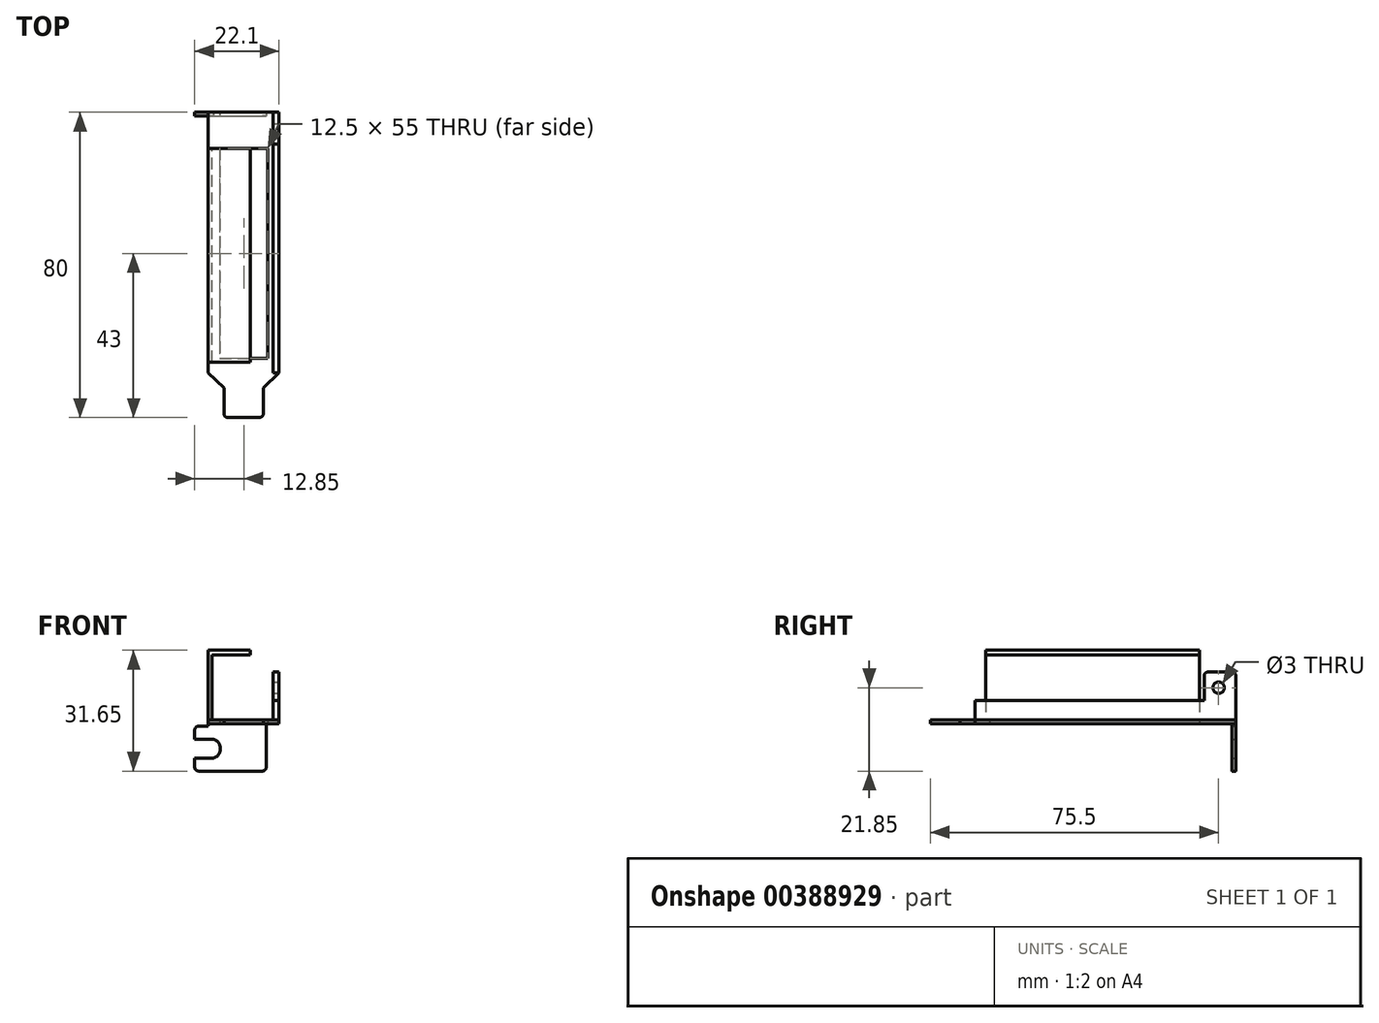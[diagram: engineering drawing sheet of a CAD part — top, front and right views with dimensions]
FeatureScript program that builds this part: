
annotation { "Feature Type Name" : "Feature", "Feature Type Description" : "" }
export const myFeature = defineFeature(function(context is Context, id is Id, definition is map)
    precondition{}
    {
        {
            var Q0;
            Q0=qCreatedBy(makeId("Top.planeOp"),FACE);
            var sketch = newSketch(context, id + "F0", { "sketchPlane" : qUnion([Q0])});
            skLineSegment(sketch, "E0", {"start": v(-1, 0) * mm, "end": v(-9.3, 0) * mm});
            skLineSegment(sketch, "E1", {"start": v(-10.3, 1) * mm, "end": v(-10.3, 7.8) * mm});
            skLineSegment(sketch, "E2", {"start": v(-10.3, 7.8) * mm, "end": v(-14.45, 11.7) * mm});
            skLineSegment(sketch, "E3", {"start": v(-14.45, 11.7) * mm, "end": v(-14.45, 73.4) * mm});
            skLineSegment(sketch, "E4", {"start": v(0, 1) * mm, "end": v(0, 7.8) * mm});
            skLineSegment(sketch, "E5", {"start": v(0, 7.8) * mm, "end": v(4.15, 11.7) * mm});
            skLineSegment(sketch, "E6", {"start": v(4.15, 11.7) * mm, "end": v(4.15, 73.4) * mm});
            skLineSegment(sketch, "E7", {"start": v(-14.45, 11.7) * mm, "end": v(4.15, 11.7) * mm, "construction": true});
            skLineSegment(sketch, "E8", {"start": v(-14.45, 73.4) * mm, "end": v(-14.45, 80) * mm});
            skLineSegment(sketch, "E9", {"start": v(-14.45, 80) * mm, "end": v(0.75, 80) * mm});
            skLineSegment(sketch, "E10", {"start": v(-14.45, 80) * mm, "end": v(-47.1, 80) * mm, "construction": true});
            skLineSegment(sketch, "E11", {"start": v(-47.1, 80) * mm, "end": v(-47.1, 0) * mm, "construction": true});
            skLineSegment(sketch, "E12", {"start": v(-47.1, 0) * mm, "end": v(-10.3, 0) * mm, "construction": true});
            skLineSegment(sketch, "E13", {"start": v(-14.45, 11.7) * mm, "end": v(-37.1, 11.7) * mm, "construction": true});
            skLineSegment(sketch, "E14", {"start": v(-37.1, 11.7) * mm, "end": v(-37.1, 80) * mm, "construction": true});
            skLineSegment(sketch, "E15", {"start": v(0.75, 80) * mm, "end": v(0.75, 76.5) * mm});
            skLineSegment(sketch, "E16", {"start": v(0.75, 76.5) * mm, "end": v(4.15, 73.4) * mm});
            skPoint(sketch, "E17.visualSharp", {"position": v(0, 0) * mm});
            skArc(sketch, "E17.filletArc", {"start": v(-1, 0) * mm, "mid": v(-0.3, 0.3) * mm, "end": v(0, 1) * mm});
            skPoint(sketch, "E18.visualSharp", {"position": v(-10.3, 0) * mm});
            skArc(sketch, "E18.filletArc", {"start": v(-10.3, 1) * mm, "mid": v(-10, 0.3) * mm, "end": v(-9.3, 0) * mm});
            skLineSegment(sketch, "E19", {"start": v(4.15, 73.4) * mm, "end": v(4.15, 80) * mm, "construction": true});
            skLineSegment(sketch, "E20", {"start": v(4.15, 80) * mm, "end": v(0.75, 80) * mm, "construction": true});
            skSolve(sketch);
        }
        {
            var Q0;
            Q0 = qSketchRegion(id + "F0", true);
            extrude(context, id + "F1", {"entities" : qUnion([Q0]), "depth" : 1 * mm});
        }
        {
            var Q0;
            Q0=makeQuery(id+"F1.opExtrude","SWEPT_FACE",FACE,{"disambiguationData":[OSD([sQuery(id+"F0.wireOp",EDGE,"E9")])]});
            var sketch = newSketch(context, id + "F2", { "sketchPlane" : qUnion([Q0])});
            skLineSegment(sketch, "E21", {"start": v(14.45, 1) * mm, "end": v(14.45, -0.7) * mm});
            skLineSegment(sketch, "E22", {"start": v(14.45, -0.7) * mm, "end": v(16.95, -0.7) * mm});
            skLineSegment(sketch, "E23", {"start": v(17.95, -1.7) * mm, "end": v(17.95, -4.1) * mm});
            skLineSegment(sketch, "E24", {"start": v(17.95, -4.1) * mm, "end": v(12.95, -4.1) * mm});
            skLineSegment(sketch, "E25", {"start": v(12.95, -9.05) * mm, "end": v(17.95, -9.05) * mm});
            skLineSegment(sketch, "E26", {"start": v(17.95, -9.05) * mm, "end": v(17.95, -11.45) * mm});
            skPoint(sketch, "E27", {"position": v(-0.75, 0.5) * mm});
            skLineSegment(sketch, "E28", {"start": v(16.95, -12.45) * mm, "end": v(0.25, -12.45) * mm});
            skLineSegment(sketch, "E29", {"start": v(-0.75, -11.45) * mm, "end": v(-0.75, 1) * mm});
            skLineSegment(sketch, "E30", {"start": v(11.25, -6.57) * mm, "end": v(11.25, -2.4) * mm, "construction": true});
            skLineSegment(sketch, "E31", {"start": v(11.25, -2.4) * mm, "end": v(17.95, -2.4) * mm, "construction": true});
            skArc(sketch, "E32", {"start": v(12.95, -4.1) * mm, "mid": v(11.25, -6.58) * mm, "end": v(12.95, -9.05) * mm});
            skPoint(sketch, "E33.visualSharp", {"position": v(17.95, -0.7) * mm});
            skArc(sketch, "E33.filletArc", {"start": v(17.95, -1.7) * mm, "mid": v(17.66, -1) * mm, "end": v(16.95, -0.7) * mm});
            skPoint(sketch, "E34.visualSharp", {"position": v(17.95, -12.45) * mm});
            skArc(sketch, "E34.filletArc", {"start": v(16.95, -12.45) * mm, "mid": v(17.66, -12.16) * mm, "end": v(17.95, -11.45) * mm});
            skPoint(sketch, "E35.visualSharp", {"position": v(-0.75, -12.45) * mm});
            skArc(sketch, "E35.filletArc", {"start": v(-0.75, -11.45) * mm, "mid": v(-0.46, -12.16) * mm, "end": v(0.25, -12.45) * mm});
            skLineSegment(sketch, "E36", {"start": v(-0.75, -9.25) * mm, "end": v(2.45, -9.25) * mm, "construction": true});
            skLineSegment(sketch, "E37", {"start": v(2.45, -9.25) * mm, "end": v(2.45, -12.45) * mm, "construction": true});
            skCircle(sketch, "E38", {"center": v(2.45, -9.25) * mm, "radius": 1.15 * mm});
            skSolve(sketch);
        }
        {
            var Q0;
            Q0 = qSketchRegion(id + "F2", true);
            var Q1;
            {var subQ4=sQuery(id+"F2.wireOp",EDGE,"E22");Q1=makeQuery(id+"F2.imprint","IMPRINT",FACE,{"disambiguationData":[TD([[makeQuery(id+"F2.imprint","IMPRINT",EDGE,{"derivedFrom":subQ4}),-1.0]])]});}
            extrude(context, id + "F3", {"entities" : qUnion([Q0, Q1]), "operationType" : NewBodyOperationType.ADD, "oppositeDirection" : true, "depth" : 1 * mm});
        }
        {
            var Q0;
            Q0=makeQuery(id+"F1.opExtrude","CAP_FACE",FACE,{"disambiguationData":[OSD([sQuery(id+"F0.wireOp",EDGE,"E0"),sQuery(id+"F0.wireOp",EDGE,"E1"),sQuery(id+"F0.wireOp",EDGE,"E2"),sQuery(id+"F0.wireOp",EDGE,"E3"),sQuery(id+"F0.wireOp",EDGE,"E4"),sQuery(id+"F0.wireOp",EDGE,"E5"),sQuery(id+"F0.wireOp",EDGE,"E6"),sQuery(id+"F0.wireOp",EDGE,"E8"),sQuery(id+"F0.wireOp",EDGE,"E9"),sQuery(id+"F0.wireOp",EDGE,"E15"),sQuery(id+"F0.wireOp",EDGE,"E16"),sQuery(id+"F0.wireOp",EDGE,"E17.filletArc"),sQuery(id+"F0.wireOp",EDGE,"E18.filletArc")])],"isStart":true});
            var sketch = newSketch(context, id + "F4", { "sketchPlane" : qUnion([Q0])});
            skLineSegment(sketch, "E39.bottom", {"start": v(-11.35, -70.5) * mm, "end": v(1.15, -70.5) * mm});
            skLineSegment(sketch, "E39.top", {"start": v(-11.35, -15.5) * mm, "end": v(1.15, -15.5) * mm});
            skLineSegment(sketch, "E39.left", {"start": v(-11.35, -70.5) * mm, "end": v(-11.35, -15.5) * mm});
            skLineSegment(sketch, "E39.right", {"start": v(1.15, -70.5) * mm, "end": v(1.15, -15.5) * mm});
            skLineSegment(sketch, "E40", {"start": v(1.15, -28.24) * mm, "end": v(4.15, -28.24) * mm, "construction": true});
            skLineSegment(sketch, "E41", {"start": v(-6.24, 0) * mm, "end": v(-6.24, -15.5) * mm, "construction": true});
            skPoint(sketch, "E41.endSnap0", {"position": v(-5.1, -15.5) * mm});
            skSolve(sketch);
        }
        {
            var Q0;
            Q0=makeQuery(id+"F4.imprint","IMPRINT",FACE,{"disambiguationData":[TD([[makeQuery(id+"F4.imprint","IMPRINT",EDGE,{"derivedFrom":sQuery(id+"F4.wireOp",EDGE,"E39.bottom")}),1.0]])]});
            extrude(context, id + "F5", {"entities" : qUnion([Q0]), "operationType" : NewBodyOperationType.REMOVE, "oppositeDirection" : true, "depth" : 1 * mm});
        }
        {
            var Q0;
            Q0=makeQuery(id+"F1.opExtrude","CAP_FACE",FACE,{"disambiguationData":[OSD([sQuery(id+"F0.wireOp",EDGE,"E0"),sQuery(id+"F0.wireOp",EDGE,"E1"),sQuery(id+"F0.wireOp",EDGE,"E2"),sQuery(id+"F0.wireOp",EDGE,"E3"),sQuery(id+"F0.wireOp",EDGE,"E4"),sQuery(id+"F0.wireOp",EDGE,"E5"),sQuery(id+"F0.wireOp",EDGE,"E6"),sQuery(id+"F0.wireOp",EDGE,"E8"),sQuery(id+"F0.wireOp",EDGE,"E9"),sQuery(id+"F0.wireOp",EDGE,"E15"),sQuery(id+"F0.wireOp",EDGE,"E16"),sQuery(id+"F0.wireOp",EDGE,"E17.filletArc"),sQuery(id+"F0.wireOp",EDGE,"E18.filletArc")])],"isStart":false});
            var sketch = newSketch(context, id + "F6", { "sketchPlane" : qUnion([Q0])});
            skLineSegment(sketch, "E42", {"start": v(4.15, 73.4) * mm, "end": v(4.15, 80) * mm});
            skLineSegment(sketch, "E43", {"start": v(4.15, 80) * mm, "end": v(0.75, 80) * mm});
            skLineSegment(sketch, "E44", {"start": v(0.75, 80) * mm, "end": v(0.75, 76.5) * mm});
            skLineSegment(sketch, "E45", {"start": v(0.75, 76.5) * mm, "end": v(4.15, 73.4) * mm});
            skSolve(sketch);
        }
        {
            var Q0;
            Q0 = qSketchRegion(id + "F6", true);
            extrude(context, id + "F7", {"entities" : qUnion([Q0]), "operationType" : NewBodyOperationType.ADD, "oppositeDirection" : true, "depth" : 1 * mm});
        }
        {
            var Q0;
            Q0=makeQuery(id+"F1.opExtrude","SWEPT_FACE",FACE,{"disambiguationData":[OSD([sQuery(id+"F0.wireOp",EDGE,"E6")])]});
            var sketch = newSketch(context, id + "F8", { "sketchPlane" : qUnion([Q0])});
            skLineSegment(sketch, "E46", {"start": v(80, 1) * mm, "end": v(80, 12.5) * mm});
            skLineSegment(sketch, "E47", {"start": v(79, 13.5) * mm, "end": v(72.7, 13.5) * mm});
            skLineSegment(sketch, "E48", {"start": v(71.7, 12.5) * mm, "end": v(71.7, 6) * mm});
            skLineSegment(sketch, "E49", {"start": v(71.7, 6) * mm, "end": v(11.7, 6) * mm});
            skPoint(sketch, "E50.visualSharp", {"position": v(80, 13.5) * mm});
            skArc(sketch, "E50.filletArc", {"start": v(80, 12.5) * mm, "mid": v(79.7, 13.2) * mm, "end": v(79, 13.5) * mm});
            skPoint(sketch, "E51.visualSharp", {"position": v(71.7, 13.5) * mm});
            skArc(sketch, "E51.filletArc", {"start": v(72.7, 13.5) * mm, "mid": v(72, 13.2) * mm, "end": v(71.7, 12.5) * mm});
            skLineSegment(sketch, "E52", {"start": v(75.5, 13.5) * mm, "end": v(75.5, 9.4) * mm, "construction": true});
            skLineSegment(sketch, "E53", {"start": v(11.7, 6) * mm, "end": v(11.7, 1) * mm});
            skLineSegment(sketch, "E54", {"start": v(75.5, 9.4) * mm, "end": v(80, 9.4) * mm, "construction": true});
            skSolve(sketch);
        }
        {
            var Q0;
            {var subQ1=sQuery(id+"F8.wireOp",EDGE,"E47");Q0=makeQuery(id+"F8.imprint","IMPRINT",FACE,{"disambiguationData":[TD([[makeQuery(id+"F8.imprint","IMPRINT",EDGE,{"derivedFrom":subQ1}),1.0]])]});}
            extrude(context, id + "F9", {"entities" : qUnion([Q0]), "oppositeDirection" : true, "depth" : 1.6 * mm});
        }
        {
            var Q0;
            Q0=makeQuery(id+"F7.boolean.opBoolean","MERGE",FACE,{"derivedFrom":[makeQuery(id+"F1.opExtrude","CAP_FACE",FACE,{"disambiguationData":[OSD([sQuery(id+"F0.wireOp",EDGE,"E0"),sQuery(id+"F0.wireOp",EDGE,"E1"),sQuery(id+"F0.wireOp",EDGE,"E2"),sQuery(id+"F0.wireOp",EDGE,"E3"),sQuery(id+"F0.wireOp",EDGE,"E4"),sQuery(id+"F0.wireOp",EDGE,"E5"),sQuery(id+"F0.wireOp",EDGE,"E6"),sQuery(id+"F0.wireOp",EDGE,"E8"),sQuery(id+"F0.wireOp",EDGE,"E9"),sQuery(id+"F0.wireOp",EDGE,"E15"),sQuery(id+"F0.wireOp",EDGE,"E16"),sQuery(id+"F0.wireOp",EDGE,"E17.filletArc"),sQuery(id+"F0.wireOp",EDGE,"E18.filletArc")])],"isStart":false}),makeQuery(id+"F7.opExtrude","CAP_FACE",FACE,{"disambiguationData":[OSD([sQuery(id+"F6.wireOp",EDGE,"E42"),sQuery(id+"F6.wireOp",EDGE,"E43"),sQuery(id+"F6.wireOp",EDGE,"E44"),sQuery(id+"F6.wireOp",EDGE,"E45")])],"isStart":true})]});
            var sketch = newSketch(context, id + "F10", { "sketchPlane" : qUnion([Q0])});
            skLineSegment(sketch, "E55.bottom", {"start": v(-14.45, 14.5) * mm, "end": v(-13.45, 14.5) * mm});
            skLineSegment(sketch, "E55.top", {"start": v(-14.45, 70.5) * mm, "end": v(-13.45, 70.5) * mm});
            skLineSegment(sketch, "E55.left", {"start": v(-14.45, 14.5) * mm, "end": v(-14.45, 70.5) * mm});
            skLineSegment(sketch, "E55.right", {"start": v(-13.45, 14.5) * mm, "end": v(-13.45, 70.5) * mm});
            skLineSegment(sketch, "E56", {"start": v(-11.35, 70.5) * mm, "end": v(-14.45, 70.5) * mm, "construction": true});
            skSolve(sketch);
        }
        {
            var Q0;
            Q0 = qSketchRegion(id + "F10", true);
            extrude(context, id + "F11", {"entities" : qUnion([Q0]), "operationType" : NewBodyOperationType.ADD, "depth" : 18.2 * mm, "offsetDistance" : 25 * mm});
        }
        {
            var Q0;
            Q0=sQuery(id+"F8.wireOp",VERTEX,"E54.start");
            var Q1;
            Q1=makeQuery(id+"F9.opExtrude","SWEPT_BODY",BODY,{"disambiguationData":[OSD([sQuery(id+"F0.wireOp",EDGE,"E6"),sQuery(id+"F8.wireOp",EDGE,"E46"),sQuery(id+"F8.wireOp",EDGE,"E47"),sQuery(id+"F8.wireOp",EDGE,"E48"),sQuery(id+"F8.wireOp",EDGE,"E49"),sQuery(id+"F8.wireOp",EDGE,"CeXhadmo-0k7W-pfPG-MfyN-3bJz2qx1B6s9"),sQuery(id+"F8.wireOp",EDGE,"E50.filletArc"),sQuery(id+"F8.wireOp",EDGE,"E51.filletArc")])]});
            hole(context, id + "F12", {"style" : HoleStyle.SIMPLE, "endStyle" : HoleEndStyle.THROUGH, "holeDiameter" : 3 * mm, "majorDiameter" : 5 * mm, "isTappedThrough" : true, "tappedDepth" : 12 * mm, "tapClearance" : 3, "locations" : qUnion([Q0]), "scope" : qUnion([Q1])});
        }
        {
            var Q0;
            Q0=makeQuery(id+"F11.opExtrude","SWEPT_FACE",FACE,{"disambiguationData":[OSD([sQuery(id+"F10.wireOp",EDGE,"E55.right")])]});
            var sketch = newSketch(context, id + "F13", { "sketchPlane" : qUnion([Q0])});
            skLineSegment(sketch, "E57.bottom", {"start": v(14.5, 19.2) * mm, "end": v(70.5, 19.2) * mm});
            skLineSegment(sketch, "E57.top", {"start": v(14.5, 18) * mm, "end": v(70.5, 18) * mm});
            skLineSegment(sketch, "E57.left", {"start": v(14.5, 19.2) * mm, "end": v(14.5, 18) * mm});
            skLineSegment(sketch, "E57.right", {"start": v(70.5, 19.2) * mm, "end": v(70.5, 18) * mm});
            skSolve(sketch);
        }
        {
            var Q0;
            Q0 = qSketchRegion(id + "F13", true);
            extrude(context, id + "F14", {"entities" : qUnion([Q0]), "operationType" : NewBodyOperationType.ADD, "depth" : 10 * mm});
        }
    });
